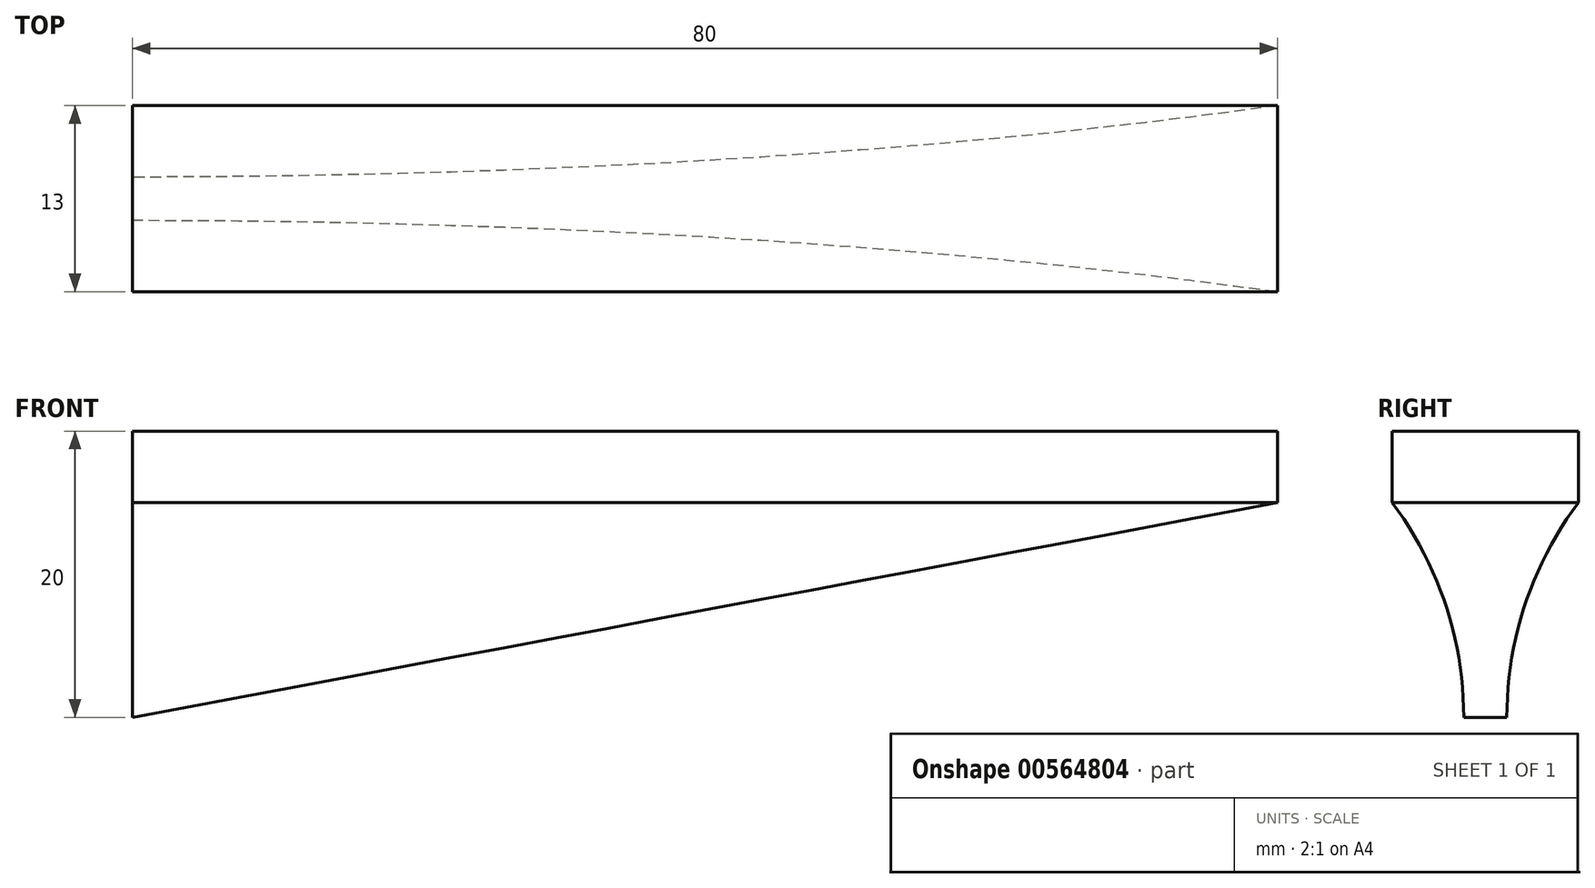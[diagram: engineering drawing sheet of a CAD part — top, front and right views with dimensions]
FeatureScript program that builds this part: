
annotation { "Feature Type Name" : "Feature", "Feature Type Description" : "" }
export const myFeature = defineFeature(function(context is Context, id is Id, definition is map)
    precondition{}
    {
        {
            var Q0;
            Q0=qCreatedBy(makeId("Front.planeOp"),FACE);
            var sketch = newSketch(context, id + "F0", { "sketchPlane" : qUnion([Q0])});
            skLineSegment(sketch, "E0", {"start": v(0, 0) * mm, "end": v(80, 0) * mm});
            skLineSegment(sketch, "E1", {"start": v(80, 0) * mm, "end": v(80, -5) * mm});
            skLineSegment(sketch, "E2", {"start": v(80, -5) * mm, "end": v(0, -20) * mm});
            skLineSegment(sketch, "E3", {"start": v(0, -20) * mm, "end": v(0, 0) * mm});
            skSolve(sketch);
        }
        {
            var Q0;
            Q0 = qSketchRegion(id + "F0", true);
            extrude(context, id + "F1", {"entities" : qUnion([Q0]), "endBound" : BoundingType.SYMMETRIC, "depth" : 13 * mm, "offsetDistance" : 25 * mm});
        }
        {
            var Q0;
            Q0=qCreatedBy(makeId("Right.planeOp"),FACE);
            var sketch = newSketch(context, id + "F2", { "sketchPlane" : qUnion([Q0])});
            skLineSegment(sketch, "E4", {"start": v(-6.5, 0) * mm, "end": v(6.5, 0) * mm});
            skLineSegment(sketch, "E5", {"start": v(6.5, 0) * mm, "end": v(6.5, -5) * mm});
            skLineSegment(sketch, "E6", {"start": v(1.5, -20) * mm, "end": v(-1.5, -20) * mm});
            skLineSegment(sketch, "E7", {"start": v(-6.5, -5) * mm, "end": v(-6.5, 0) * mm});
            skPoint(sketch, "E8", {"position": v(0, 0) * mm});
            skPoint(sketch, "E9", {"position": v(0, -20) * mm});
            skArc(sketch, "E10", {"start": v(-1.5, -20) * mm, "mid": v(-2.78, -12.1) * mm, "end": v(-6.5, -5) * mm});
            skArc(sketch, "E11.MirrorCS", {"start": v(1.5, -20) * mm, "mid": v(2.78, -12.1) * mm, "end": v(6.5, -5) * mm});
            skSolve(sketch);
        }
        {
            var Q0;
            Q0 = qSketchRegion(id + "F2", true);
            extrude(context, id + "F3", {"entities" : qUnion([Q0]), "operationType" : NewBodyOperationType.INTERSECT, "depth" : 80 * mm, "offsetDistance" : 25 * mm});
        }
    });
